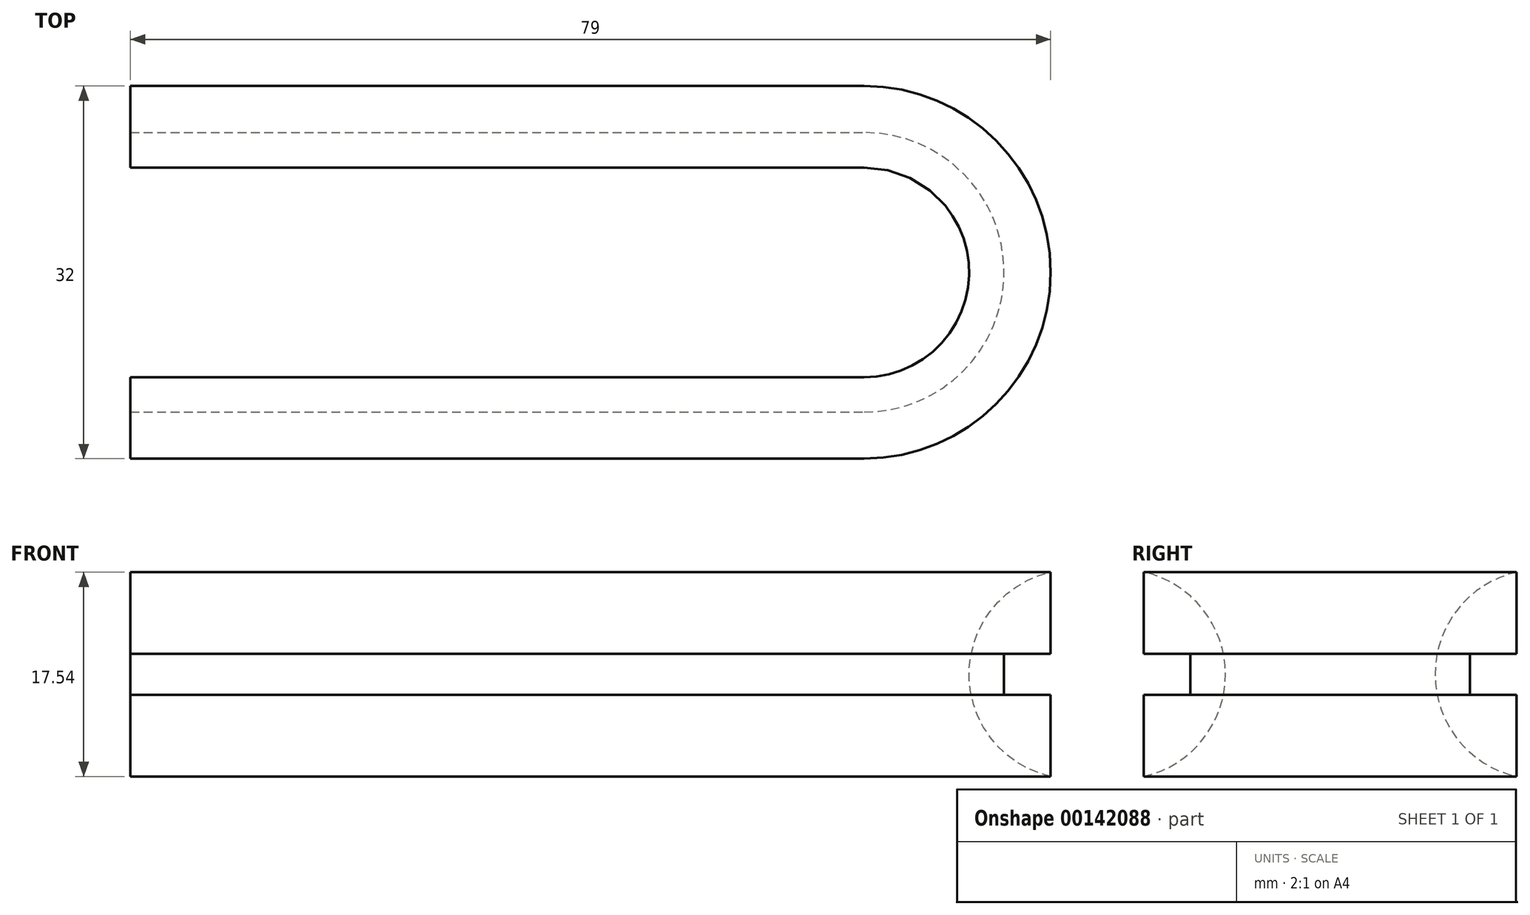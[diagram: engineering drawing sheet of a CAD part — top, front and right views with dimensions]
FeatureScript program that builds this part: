
annotation { "Feature Type Name" : "Feature", "Feature Type Description" : "" }
export const myFeature = defineFeature(function(context is Context, id is Id, definition is map)
    precondition{}
    {
        {
            var Q0;
            Q0=qCreatedBy(makeId("Top.planeOp"),FACE);
            var sketch = newSketch(context, id + "F0", { "sketchPlane" : qUnion([Q0])});
            skArc(sketch, "E0", {"start": v(75, 0) * mm, "mid": v(71.49, 8.49) * mm, "end": v(63, 12) * mm});
            skLineSegment(sketch, "E1", {"start": v(63, 12) * mm, "end": v(0, 12) * mm});
            skSolve(sketch);
        }
        {
            var Q0;
            Q0=qCreatedBy(makeId("Right.planeOp"),FACE);
            var sketch = newSketch(context, id + "F1", { "sketchPlane" : qUnion([Q0])});
            skLineSegment(sketch, "E2", {"start": v(16, -3.5) * mm, "end": v(16, -10.52) * mm});
            skArc(sketch, "E3.MirrorCS", {"start": v(16, -10.52) * mm, "mid": v(9, -1.75) * mm, "end": v(16, 7.02) * mm});
            skLineSegment(sketch, "E4.MirrorCS", {"start": v(16, 0) * mm, "end": v(12, 0) * mm});
            skLineSegment(sketch, "E5.MirrorCS", {"start": v(12, 0) * mm, "end": v(12, -3.5) * mm});
            skLineSegment(sketch, "E6.MirrorCS", {"start": v(16, -3.5) * mm, "end": v(12, -3.5) * mm});
            skLineSegment(sketch, "E7", {"start": v(16, 0) * mm, "end": v(16, 7.02) * mm});
            skSolve(sketch);
        }
        {
            var Q0;
            Q0=makeQuery(id+"F1.imprint","IMPRINT",FACE,{"disambiguationData":[TD([[makeQuery(id+"F1.imprint","IMPRINT",EDGE,{"derivedFrom":sQuery(id+"F1.wireOp",EDGE,"E2")}),-1.0]])]});
            var Q1;
            Q1=sQuery(id+"F0.wireOp",EDGE,"E1");
            var Q2;
            Q2=sQuery(id+"F0.wireOp",EDGE,"E0");
            sweep(context, id + "F2", {"profiles" : qUnion([Q0]), "path" : qUnion([Q1, Q2])});
        }
        {
            var Q0;
            Q0=makeQuery(id+"F2.opSweep","SWEPT_BODY",BODY,{"disambiguationData":[OSD([sQuery(id+"F0.wireOp",EDGE,"E0"),sQuery(id+"F1.wireOp",EDGE,"E2"),sQuery(id+"F1.wireOp",EDGE,"E3.MirrorCS"),sQuery(id+"F1.wireOp",EDGE,"E4.MirrorCS"),sQuery(id+"F1.wireOp",EDGE,"E5.MirrorCS"),sQuery(id+"F1.wireOp",EDGE,"E6.MirrorCS"),sQuery(id+"F1.wireOp",EDGE,"E7")])]});
            var Q1;
            Q1=makeQuery(id+"F2.opSweep","CAP_FACE",FACE,{"disambiguationData":[OSD([sQuery(id+"F0.wireOp",VERTEX,"E0.start"),sQuery(id+"F1.wireOp",EDGE,"E2"),sQuery(id+"F1.wireOp",EDGE,"E3.MirrorCS"),sQuery(id+"F1.wireOp",EDGE,"E4.MirrorCS"),sQuery(id+"F1.wireOp",EDGE,"E5.MirrorCS"),sQuery(id+"F1.wireOp",EDGE,"E6.MirrorCS"),sQuery(id+"F1.wireOp",EDGE,"E7")])],"isStart":false});
            mirror(context, id + "F3", {"operationType" : NewBodyOperationType.ADD, "entities" : qUnion([Q0]), "mirrorPlane" : qUnion([Q1])});
        }
    });
